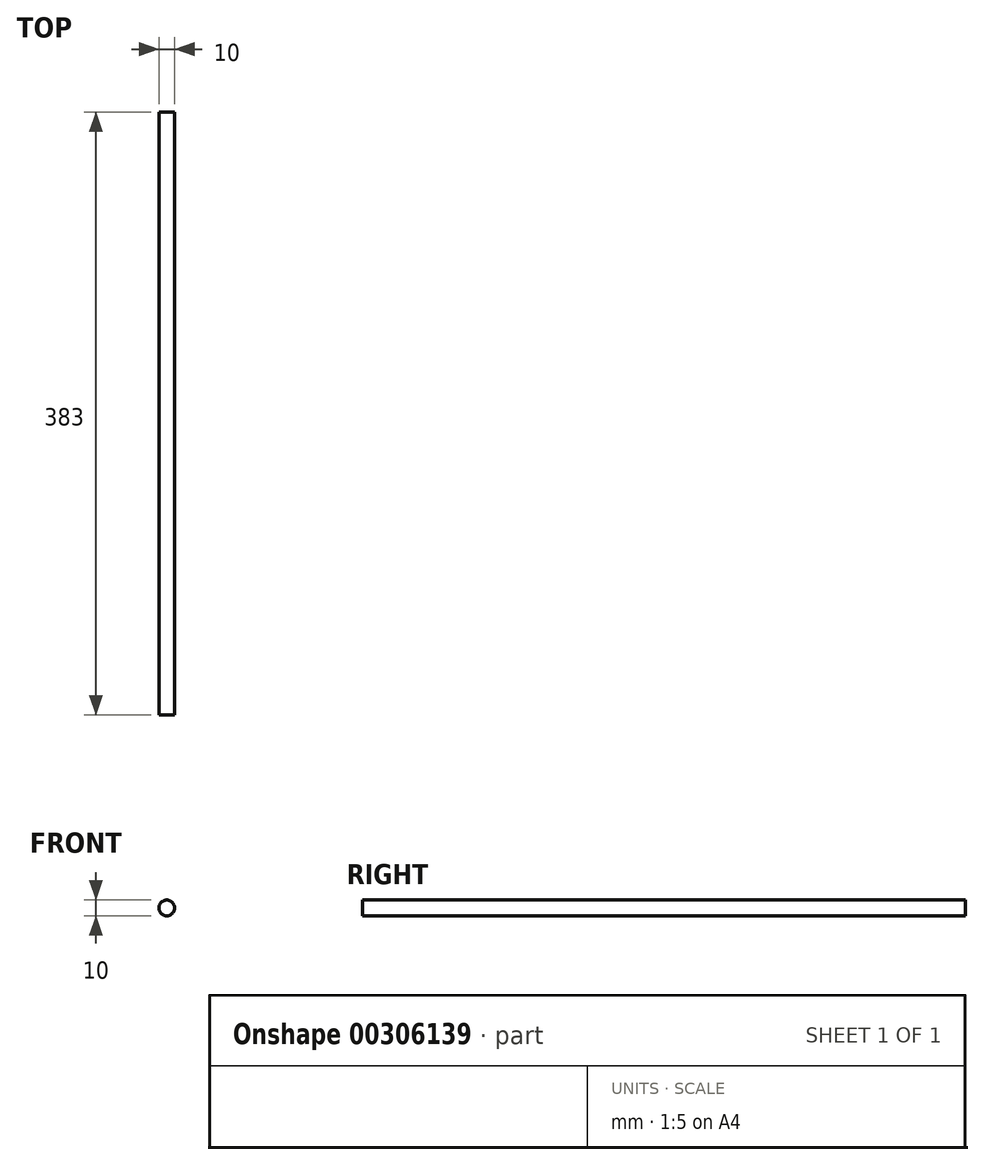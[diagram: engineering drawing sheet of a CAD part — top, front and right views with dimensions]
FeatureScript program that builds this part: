
annotation { "Feature Type Name" : "Feature", "Feature Type Description" : "" }
export const myFeature = defineFeature(function(context is Context, id is Id, definition is map)
    precondition{}
    {
        {
            var Q0;
            Q0=qCreatedBy(makeId("Front.planeOp"),FACE);
            var sketch = newSketch(context, id + "F0", { "sketchPlane" : qUnion([Q0])});
            skCircle(sketch, "E0", {"center": v(0, 0) * mm, "radius": 5 * mm});
            skSolve(sketch);
        }
        {
            var Q0;
            Q0=makeQuery(id+"F0.imprint","IMPRINT",FACE,{"disambiguationData":[TD([[makeQuery(id+"F0.imprint","IMPRINT",EDGE,{"derivedFrom":sQuery(id+"F0.wireOp",EDGE,"E0")}),1.0]])]});
            extrude(context, id + "F1", {"entities" : qUnion([Q0]), "oppositeDirection" : true, "depth" : 383 * mm});
        }
    });
